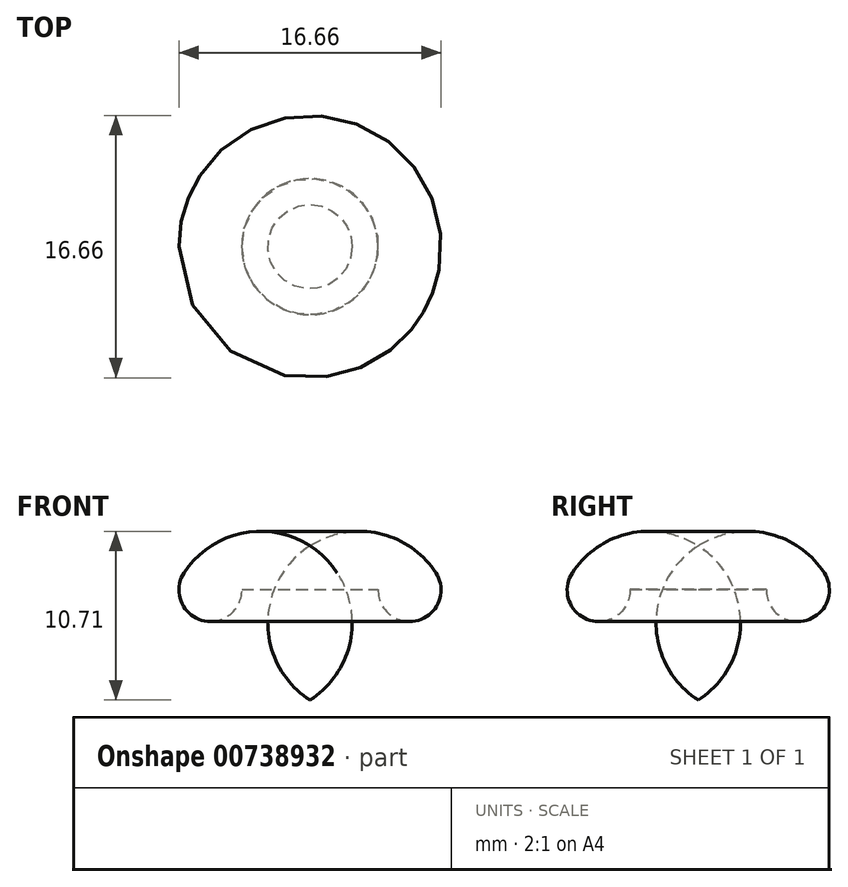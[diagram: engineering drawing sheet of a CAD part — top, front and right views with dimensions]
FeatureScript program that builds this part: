
annotation { "Feature Type Name" : "Feature", "Feature Type Description" : "" }
export const myFeature = defineFeature(function(context is Context, id is Id, definition is map)
    precondition{}
    {
        {
            var Q0;
            Q0=qCreatedBy(makeId("Top.planeOp"),FACE);
            var sketch = newSketch(context, id + "F0", { "sketchPlane" : qUnion([Q0])});
            skCircle(sketch, "E0", {"center": v(0, 0) * mm, "radius": 8 * mm});
            skSolve(sketch);
        }
        {
            var Q0;
            Q0=qCreatedBy(makeId("Front.planeOp"),FACE);
            var sketch = newSketch(context, id + "F1", { "sketchPlane" : qUnion([Q0])});
            skArc(sketch, "E1", {"start": v(0, 1.71) * mm, "mid": v(-4.35, 2.5) * mm, "end": v(-8, 0) * mm});
            skLineSegment(sketch, "E2", {"start": v(0, 0) * mm, "end": v(0, 41.65) * mm, "construction": true});
            skLineSegment(sketch, "E3", {"start": v(-8, 0) * mm, "end": v(0, 0) * mm});
            skLineSegment(sketch, "E4", {"start": v(0, 1.71) * mm, "end": v(0, 0) * mm});
            skArc(sketch, "E5", {"start": v(-8, 0) * mm, "mid": v(-6.87, -3.02) * mm, "end": v(-4.33, -1.05) * mm});
            skLineSegment(sketch, "E6", {"start": v(-4.33, -1.05) * mm, "end": v(0, -1.05) * mm});
            skLineSegment(sketch, "E7", {"start": v(0, -1.05) * mm, "end": v(0, 0) * mm});
            skSolve(sketch);
        }
        {
            var Q0;
            Q0=makeQuery(id+"F1.imprint","IMPRINT",FACE,{"disambiguationData":[TD([[makeQuery(id+"F1.imprint","IMPRINT",EDGE,{"derivedFrom":sQuery(id+"F1.wireOp",EDGE,"E1")}),1.0]])]});
            var Q1;
            Q1=makeQuery(id+"F1.imprint","IMPRINT",FACE,{"disambiguationData":[TD([[makeQuery(id+"F1.imprint","IMPRINT",EDGE,{"derivedFrom":sQuery(id+"F1.wireOp",EDGE,"E3")}),-1.0]])]});
            var Q2;
            Q2=sQuery(id+"F1.wireOp",EDGE,"E2");
            revolve(context, id + "F2", {"surfaceOperationType" : NewSurfaceOperationType.NEW, "entities" : qUnion([Q0, Q1]), "axis" : qUnion([Q2]), "revolveType" : RevolveType.FULL});
        }
    });
